# Revit family: Toilet-Floor_Mount-KOHLER-Odeon_Up-K-76186LM_1
name_source: partatom
category: Plumbing Fixtures
revit_build: Autodesk Revit 2015 (Build: 20140606_1530(x64)
units: mm (PartAtom-declared; Revit-internal decimal feet)

## types (1)
- 0-White
    ADA Compliant = No
    Assembly Code = D2010100
    CW Connection = Yes
    Cold Water Inlet = Cold Water Inlet
    Date Modified = 08/05/2019
    Default Elevation = 0"
    Description = Close-Coupled Dual Flush 3/6L Washdown Toilet with S-trap
    Finish = Kohler-Vitreous_China-0-White
    Flow Rate = 0 GPM
    Flush Rate- GPF = 1.6 GPF
    Flush Rate- LPF = 6 LPF
    HW Connection = No
    Height = 31 3/8"
    Hot Water Inlet = Hot Water Inlet
    Length = 25 5/8"
    Manufacturer = KOHLER Co.
    MasterFormat 1995 = 15410
    MasterFormat 2004 = 22.41.13
    Material = Vitreous China
    Model = K-76186LM-0
    Pressure = 0.00 psi
    Product Documentation Link = http://resources.kohler.com
    Product Name = Odeon Up
    Product Page URL = https://la.kohler.com
    Rough-In = 12"
    Seat Included = Yes
    URL = https://la.kohler.com
    Vent Connection = No
    Waste Connection = Yes
    Waste Water Outlet = Waste Water Outlet
    WaterSense Certified = No
    Width = 16"

## geometry (parser evidence)
native form markers: Sweep x5
no freeform markers — native parametric forms only
